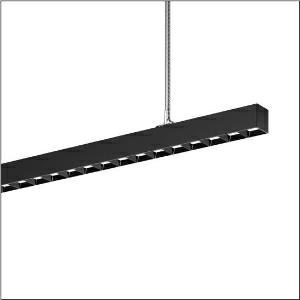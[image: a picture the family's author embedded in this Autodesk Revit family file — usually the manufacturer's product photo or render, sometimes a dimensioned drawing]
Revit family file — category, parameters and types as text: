
# Revit family: silica_r__21_51mx34dc4dbb_b20b
name_source: partatom
category: Lighting Fixtures
units: mm (PartAtom-declared; Revit-internal decimal feet)

## family parameters
Cut with Voids When Loaded = No
Host = Face
Light Source = No
Part Type = Normal
Room Calculation Point = No
Round Connector Dimension = Use Diameter
Shared = No

## types (1)
- --- (1 x LED, 19200 lm, 120.3 W, 4000K)
    Apparent Load = 120 VA
    CIE Flux Codes = 74 94 99 56 100
    Color Rendering = 80
    Color Temperature = 4000K
    Default Elevation = 1800 mm
    Description = Silica® 21, office luminaire, primary light control with darklight reflector, of PMMA, black, light emission: direct/indirect distribution, primary light characteristic: asymmetric, installation type: suspended mounting, LED, rated luminous flux: 19.200lm, luminous efficacy: 160lm/W, light colour: 840, colour temperature: 4000K, with terminal, 3+2-pole, max. 2.5mm², mains connection: 220..240V, AC, 50/60Hz, rated input power: 120.3W, luminaire housing, of aluminium, jet black (RAL 9005), length: 3.004mm, width: 53mm, height: 53mm, protection rating (complete): IP20, insulation class (complete): insulation class I (protective earthing), certification: CE, permissible operating ambient temperature: 0..+35°C, standard: EN 50419, packaging unit: 1 piece
    Height = 53 mm
    Lamp = 1 x LED
    Lamp Light Flux = 19200 lm
    Lamp Power = 120.3 W
    Lamp count = 1
    Length = 3004 mm
    Luminous efficacy = 160 lm/W
    Manufacturer = Siteco
    ModVariant = No
    Model = 51MX34DC4DBB
    Mounting Place = Ceiling
    Mounting Type = Pendant
    Number of Poles = 1
    OnlyDefault = Yes
    Power Factor = 1
    Product Name = Silica® 21
    Product group = office luminaire | ceiling pendant
    ProductGroupID = 902
    Protection Class = Protection class I
    Protection Degree = IP 20
    RLX_Detail_Level = 1
    RLX_Emergency_Light_Flux = 0 lm
    RLX_Emergency_Type = 0
    RLX_Emergency_Type_DB = No
    RlxData = <blob elided: 66945 chars, md5=e2dc8514>
    Socket = socket
    Standby Power = 0 W
    System Light Flux = 19200 lm
    System Power = 120 W
    Type Comments = factory setting: luminous flux: 100 % | dim-lin: 254 | 418 mA
    Type Image = l_1313617.jpg
    URL = http://relux.com
    VarID = @adj_068947
    Voltage = 0 V
    Weight = 0.00 kg
    Width = 53 mm

## geometry (parser evidence)
native form markers: Blend x4, Sweep x11
no freeform markers — native parametric forms only
